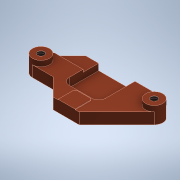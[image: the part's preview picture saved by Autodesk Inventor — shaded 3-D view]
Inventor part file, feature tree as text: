
AUTODESK INVENTOR PART (.ipt)
format: ipt  version: 2021 (Build 250183000, 183)  size: 184,832 bytes
history: native  units: mm
features: extrude x5, sketch x1, hole x1
ambient origin geometry x8: Origin, YZ Plane, XZ Plane, XY Plane, X Axis, Y Axis, Z Axis, Center Point
bodies: Solid1 (feature_tree)
feature tree (7):
  sketch  "Sketch1"  dims[d0=6.5mm d1=1.0mm d2=5.9mm d3=2.15mm d4=7.5mm d5=3.0mm d6=2.0mm d7=2.2mm d8=4.0mm d9=11.1mm d10=2.4mm d11=11.3mm d12=1.7mm d16=0.5mm d17=0.5mm d18=3.9mm d19=0.0mm d20=10.5mm d21=6.4mm d22=3.0mm d23=135.0deg d24=1.6mm d25=0.5mm d26=3.4mm d27=0.0mm d28=3.0mm d29=1.9mm d30=0.0mm d31=1.3mm d32=0.0mm d33=1.185mm d34=0.0mm d35=1.567mm d36=4.0mm d37=4.0mm d38=2.0mm d39=90.0deg d40=6.3mm d41=20.594885mm]
  extrude  "Extrusion1"  Depth=2.0mm
  extrude  "Extrusion2"  Depth=2.0mm
  extrude  "Extrusion3"  Depth=2.0mm
  extrude  "Extrusion4"  Depth=2.0mm
  extrude  "Extrusion5"  Depth=2.0mm
  hole  "Hole1"  [1 undecoded]
note: 1 required parameter value undecoded (feature->parameter linkage not recoverable at this tier; creation-order binding heuristic only, values carry confidence <= 0.55)
